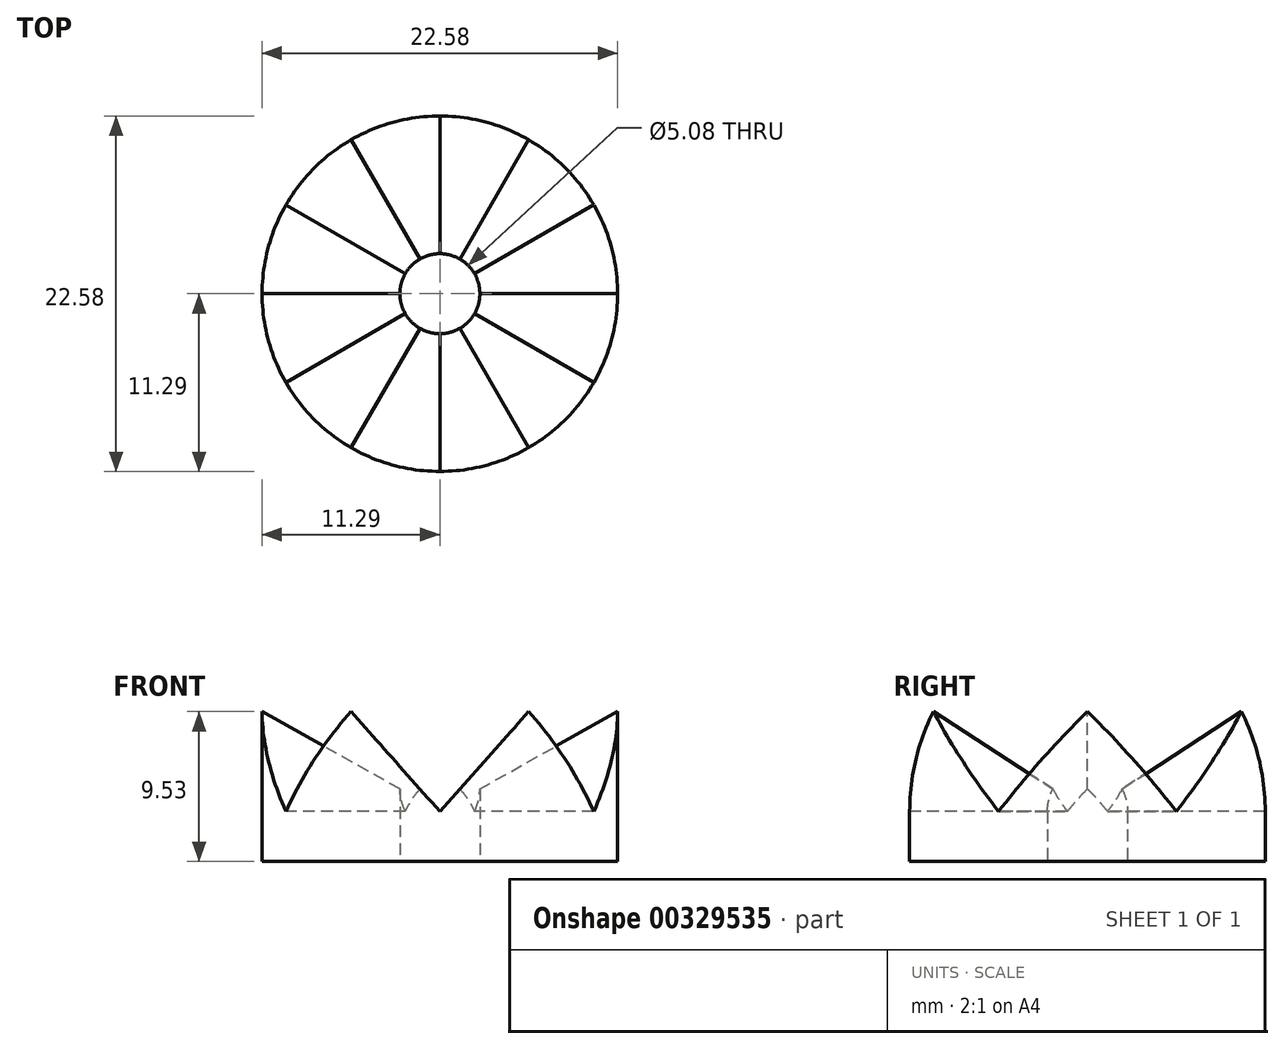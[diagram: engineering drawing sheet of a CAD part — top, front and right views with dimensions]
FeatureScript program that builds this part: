
annotation { "Feature Type Name" : "Feature", "Feature Type Description" : "" }
export const myFeature = defineFeature(function(context is Context, id is Id, definition is map)
    precondition{}
    {
        {
            var Q0;
            Q0=qCreatedBy(makeId("Top.planeOp"),FACE);
            var sketch = newSketch(context, id + "F0", { "sketchPlane" : qUnion([Q0])});
            skCircle(sketch, "E0.cCircle", {"center": v(0, 0) * mm, "radius": 11.3 * mm, "construction": true});
            skLineSegment(sketch, "E0.0", {"start": v(11.3, 0) * mm, "end": v(5.65, -9.78) * mm});
            skLineSegment(sketch, "E0.1", {"start": v(5.65, -9.78) * mm, "end": v(-5.65, -9.78) * mm});
            skLineSegment(sketch, "E0.2", {"start": v(-5.65, -9.78) * mm, "end": v(-11.3, 0) * mm});
            skLineSegment(sketch, "E0.3", {"start": v(-11.3, 0) * mm, "end": v(-5.65, 9.78) * mm});
            skLineSegment(sketch, "E0.4", {"start": v(-5.65, 9.78) * mm, "end": v(5.65, 9.78) * mm});
            skLineSegment(sketch, "E0.5", {"start": v(5.65, 9.78) * mm, "end": v(11.3, 0) * mm});
            skLineSegment(sketch, "E1", {"start": v(-5.65, -9.78) * mm, "end": v(5.65, 9.78) * mm});
            skLineSegment(sketch, "E2", {"start": v(11.3, 0) * mm, "end": v(-11.3, 0) * mm});
            skLineSegment(sketch, "E3", {"start": v(5.65, -9.78) * mm, "end": v(-5.65, 9.78) * mm});
            skCircle(sketch, "E4", {"center": v(0, 0) * mm, "radius": 11.3 * mm});
            skSolve(sketch);
        }
        {
            var Q0;
            {var subQ0=sQuery(id+"F0.wireOp",EDGE,"E0.3");Q0=makeQuery(id+"F0.imprint","IMPRINT",FACE,{"disambiguationData":[TD([[makeQuery(id+"F0.imprint","IMPRINT",EDGE,{"derivedFrom":subQ0}),-1.0]])]});}
            var Q1;
            {var subQ0=sQuery(id+"F0.wireOp",EDGE,"E0.2");Q1=makeQuery(id+"F0.imprint","IMPRINT",FACE,{"disambiguationData":[TD([[makeQuery(id+"F0.imprint","IMPRINT",EDGE,{"derivedFrom":subQ0}),-1.0]])]});}
            var Q2;
            {var subQ0=sQuery(id+"F0.wireOp",EDGE,"E0.1");Q2=makeQuery(id+"F0.imprint","IMPRINT",FACE,{"disambiguationData":[TD([[makeQuery(id+"F0.imprint","IMPRINT",EDGE,{"derivedFrom":subQ0}),-1.0]])]});}
            var Q3;
            {var subQ0=sQuery(id+"F0.wireOp",EDGE,"E0.5");Q3=makeQuery(id+"F0.imprint","IMPRINT",FACE,{"disambiguationData":[TD([[makeQuery(id+"F0.imprint","IMPRINT",EDGE,{"derivedFrom":subQ0}),-1.0]])]});}
            var Q4;
            {var subQ0=sQuery(id+"F0.wireOp",EDGE,"E0.0");Q4=makeQuery(id+"F0.imprint","IMPRINT",FACE,{"disambiguationData":[TD([[makeQuery(id+"F0.imprint","IMPRINT",EDGE,{"derivedFrom":subQ0}),-1.0]])]});}
            var Q5;
            {var subQ0=sQuery(id+"F0.wireOp",EDGE,"E0.4");Q5=makeQuery(id+"F0.imprint","IMPRINT",FACE,{"disambiguationData":[TD([[makeQuery(id+"F0.imprint","IMPRINT",EDGE,{"derivedFrom":subQ0}),-1.0]])]});}
            extrude(context, id + "F1", {"entities" : qUnion([Q0, Q1, Q2, Q3, Q4, Q5]), "depth" : 6.35 * mm, "hasSecondDirection" : true, "secondDirectionOppositeDirection" : true, "secondDirectionDepth" : 3.17 * mm});
        }
        {
            var Q0;
            Q0=makeQuery(id+"F1.opExtrude","SWEPT_FACE",FACE,{"disambiguationData":[OSD([sQuery(id+"F0.wireOp",EDGE,"E0.1")])]});
            var sketch = newSketch(context, id + "F2", { "sketchPlane" : qUnion([Q0])});
            skLineSegment(sketch, "E5", {"start": v(0, 6.35) * mm, "end": v(0, 0) * mm});
            skLineSegment(sketch, "E6", {"start": v(0, 0) * mm, "end": v(5.65, 6.35) * mm});
            skLineSegment(sketch, "E7", {"start": v(5.65, 6.35) * mm, "end": v(0, 0) * mm});
            skLineSegment(sketch, "E8", {"start": v(-5.65, 6.35) * mm, "end": v(0, 0) * mm});
            skSolve(sketch);
        }
        {
            var Q0;
            {var subQ0=sQuery(id+"F2.wireOp",EDGE,"E5");Q0=makeQuery(id+"F2.imprint","IMPRINT",FACE,{"disambiguationData":[TD([[makeQuery(id+"F2.imprint","IMPRINT",EDGE,{"derivedFrom":subQ0}),1.0]])]});}
            var Q1;
            {var subQ0=sQuery(id+"F2.wireOp",EDGE,"E5");Q1=makeQuery(id+"F2.imprint","IMPRINT",FACE,{"disambiguationData":[TD([[makeQuery(id+"F2.imprint","IMPRINT",EDGE,{"derivedFrom":subQ0}),-1.0]])]});}
            extrude(context, id + "F3", {"entities" : qUnion([Q0, Q1]), "operationType" : NewBodyOperationType.REMOVE, "endBound" : BoundingType.THROUGH_ALL, "oppositeDirection" : true, "depth" : 25.4 * mm, "hasSecondDirection" : true, "secondDirectionBound" : SecondDirectionBoundingType.THROUGH_ALL, "secondDirectionOppositeDirection" : false, "secondDirectionDepth" : 25.4 * mm});
        }
        {
            var Q0;
            Q0=makeQuery(id+"F1.opExtrude","SWEPT_FACE",FACE,{"disambiguationData":[OSD([sQuery(id+"F0.wireOp",EDGE,"E0.2")])]});
            var sketch = newSketch(context, id + "F4", { "sketchPlane" : qUnion([Q0])});
            skLineSegment(sketch, "E9", {"start": v(0, 6.35) * mm, "end": v(0, 0) * mm});
            skLineSegment(sketch, "E10", {"start": v(0, 0) * mm, "end": v(5.65, 6.35) * mm});
            skLineSegment(sketch, "E11", {"start": v(5.65, 6.35) * mm, "end": v(-5.65, 6.35) * mm});
            skLineSegment(sketch, "E12", {"start": v(-5.65, 6.35) * mm, "end": v(0, 0) * mm});
            skSolve(sketch);
        }
        {
            var Q0;
            Q0=qSketchRegion(id+"F4",true);
            extrude(context, id + "F5", {"entities" : qUnion([Q0]), "operationType" : NewBodyOperationType.REMOVE, "endBound" : BoundingType.THROUGH_ALL, "oppositeDirection" : true, "depth" : 25.4 * mm, "hasSecondDirection" : true, "secondDirectionBound" : SecondDirectionBoundingType.THROUGH_ALL, "secondDirectionOppositeDirection" : false, "secondDirectionDepth" : 25.4 * mm});
        }
        {
            var Q0;
            Q0=makeQuery(id+"F1.opExtrude","SWEPT_FACE",FACE,{"disambiguationData":[OSD([sQuery(id+"F0.wireOp",EDGE,"E0.3")])]});
            var sketch = newSketch(context, id + "F6", { "sketchPlane" : qUnion([Q0])});
            skLineSegment(sketch, "E13", {"start": v(0, 6.35) * mm, "end": v(0, 0) * mm});
            skPoint(sketch, "E13.endSnap0", {"position": v(0, 6.35) * mm});
            skLineSegment(sketch, "E14", {"start": v(0, 0) * mm, "end": v(5.65, 6.35) * mm});
            skLineSegment(sketch, "E15", {"start": v(5.65, 6.35) * mm, "end": v(0, 0) * mm});
            skLineSegment(sketch, "E16", {"start": v(-5.65, 6.35) * mm, "end": v(0, 0) * mm});
            skSolve(sketch);
        }
        {
            var Q0;
            {var subQ0=sQuery(id+"F6.wireOp",EDGE,"E13");Q0=makeQuery(id+"F6.imprint","IMPRINT",FACE,{"disambiguationData":[TD([[makeQuery(id+"F6.imprint","IMPRINT",EDGE,{"derivedFrom":subQ0}),1.0]])]});}
            var Q1;
            {var subQ0=sQuery(id+"F6.wireOp",EDGE,"E13");Q1=makeQuery(id+"F6.imprint","IMPRINT",FACE,{"disambiguationData":[TD([[makeQuery(id+"F6.imprint","IMPRINT",EDGE,{"derivedFrom":subQ0}),-1.0]])]});}
            extrude(context, id + "F7", {"entities" : qUnion([Q0, Q1]), "operationType" : NewBodyOperationType.REMOVE, "endBound" : BoundingType.THROUGH_ALL, "oppositeDirection" : true, "depth" : 25.4 * mm, "hasSecondDirection" : true, "secondDirectionBound" : SecondDirectionBoundingType.THROUGH_ALL, "secondDirectionOppositeDirection" : false, "secondDirectionDepth" : 25.4 * mm});
        }
        {
            var Q0;
            {var subQ0=sQuery(id+"F0.wireOp",EDGE,"E0.3");Q0=makeQuery(id+"F0.imprint","IMPRINT",FACE,{"disambiguationData":[TD([[makeQuery(id+"F0.imprint","IMPRINT",EDGE,{"derivedFrom":subQ0}),1.0]])]});}
            var Q1;
            {var subQ0=sQuery(id+"F0.wireOp",EDGE,"E0.4");Q1=makeQuery(id+"F0.imprint","IMPRINT",FACE,{"disambiguationData":[TD([[makeQuery(id+"F0.imprint","IMPRINT",EDGE,{"derivedFrom":subQ0}),1.0]])]});}
            var Q2;
            {var subQ0=sQuery(id+"F0.wireOp",EDGE,"E0.1");Q2=makeQuery(id+"F0.imprint","IMPRINT",FACE,{"disambiguationData":[TD([[makeQuery(id+"F0.imprint","IMPRINT",EDGE,{"derivedFrom":subQ0}),1.0]])]});}
            var Q3;
            {var subQ0=sQuery(id+"F0.wireOp",EDGE,"E0.2");Q3=makeQuery(id+"F0.imprint","IMPRINT",FACE,{"disambiguationData":[TD([[makeQuery(id+"F0.imprint","IMPRINT",EDGE,{"derivedFrom":subQ0}),1.0]])]});}
            var Q4;
            {var subQ0=sQuery(id+"F0.wireOp",EDGE,"E0.0");Q4=makeQuery(id+"F0.imprint","IMPRINT",FACE,{"disambiguationData":[TD([[makeQuery(id+"F0.imprint","IMPRINT",EDGE,{"derivedFrom":subQ0}),1.0]])]});}
            var Q5;
            {var subQ0=sQuery(id+"F0.wireOp",EDGE,"E0.5");Q5=makeQuery(id+"F0.imprint","IMPRINT",FACE,{"disambiguationData":[TD([[makeQuery(id+"F0.imprint","IMPRINT",EDGE,{"derivedFrom":subQ0}),1.0]])]});}
            extrude(context, id + "F8", {"entities" : qUnion([Q0, Q1, Q2, Q3, Q4, Q5]), "operationType" : NewBodyOperationType.ADD, "depth" : 6.35 * mm, "hasSecondDirection" : true, "secondDirectionOppositeDirection" : true, "secondDirectionDepth" : 3.17 * mm});
        }
        {
            var Q0;
            Q0=makeQuery(id+"F8.opExtrude","SWEPT_FACE",FACE,{"disambiguationData":[OSD([sQuery(id+"F0.wireOp",EDGE,"E0.3")])]});
            extrude(context, id + "F9", {"entities" : qUnion([Q0]), "operationType" : NewBodyOperationType.REMOVE, "oppositeDirection" : true, "depth" : 25.4 * mm});
        }
        {
            var Q0;
            Q0=makeQuery(id+"F8.opExtrude","SWEPT_FACE",FACE,{"disambiguationData":[OSD([sQuery(id+"F0.wireOp",EDGE,"E0.4")])]});
            extrude(context, id + "F10", {"entities" : qUnion([Q0]), "operationType" : NewBodyOperationType.REMOVE, "oppositeDirection" : true, "depth" : 25.4 * mm});
        }
        {
            var Q0;
            Q0=makeQuery(id+"F8.opExtrude","SWEPT_FACE",FACE,{"disambiguationData":[OSD([sQuery(id+"F0.wireOp",EDGE,"E0.5")])]});
            extrude(context, id + "F11", {"entities" : qUnion([Q0]), "operationType" : NewBodyOperationType.REMOVE, "oppositeDirection" : true, "depth" : 25.4 * mm});
        }
        {
            var Q0;
            Q0=makeQuery(id+"F8.opExtrude","SWEPT_FACE",FACE,{"disambiguationData":[OSD([sQuery(id+"F0.wireOp",EDGE,"E0.2")])]});
            extrude(context, id + "F12", {"entities" : qUnion([Q0]), "operationType" : NewBodyOperationType.REMOVE, "oppositeDirection" : true, "depth" : 25.4 * mm});
        }
        {
            var Q0;
            Q0=makeQuery(id+"F8.opExtrude","SWEPT_FACE",FACE,{"disambiguationData":[OSD([sQuery(id+"F0.wireOp",EDGE,"E0.1")])]});
            extrude(context, id + "F13", {"entities" : qUnion([Q0]), "operationType" : NewBodyOperationType.REMOVE, "oppositeDirection" : true, "depth" : 25.4 * mm});
        }
        {
            var Q0;
            Q0=makeQuery(id+"F8.opExtrude","SWEPT_FACE",FACE,{"disambiguationData":[OSD([sQuery(id+"F0.wireOp",EDGE,"E0.0")])]});
            extrude(context, id + "F14", {"entities" : qUnion([Q0]), "operationType" : NewBodyOperationType.REMOVE, "oppositeDirection" : true, "depth" : 25.4 * mm});
        }
        {
            var Q0;
            {var subQ0=sQuery(id+"F0.wireOp",EDGE,"E4");var subQ1=sQuery(id+"F0.wireOp",EDGE,"E0.5");var subQ2=sQuery(id+"F0.wireOp",EDGE,"E0.4");var subQ3=sQuery(id+"F0.wireOp",EDGE,"E0.3");var subQ4=sQuery(id+"F0.wireOp",EDGE,"E0.2");var subQ5=sQuery(id+"F0.wireOp",EDGE,"E0.1");var subQ6=sQuery(id+"F0.wireOp",EDGE,"E0.0");Q0=makeQuery(id+"F8.boolean.opBoolean","MERGE",FACE,{"derivedFrom":[makeQuery(id+"F1.opExtrude","CAP_FACE",FACE,{"disambiguationData":[OSD([subQ6,subQ5,subQ4,subQ3,subQ2,subQ1])],"isStart":true}),makeQuery(id+"F8.opExtrude","CAP_FACE",FACE,{"disambiguationData":[OSD([subQ6,subQ0])],"isStart":true}),makeQuery(id+"F8.opExtrude","CAP_FACE",FACE,{"disambiguationData":[OSD([subQ5,subQ0])],"isStart":true}),makeQuery(id+"F8.opExtrude","CAP_FACE",FACE,{"disambiguationData":[OSD([subQ4,subQ0])],"isStart":true}),makeQuery(id+"F8.opExtrude","CAP_FACE",FACE,{"disambiguationData":[OSD([subQ3,subQ0])],"isStart":true}),makeQuery(id+"F8.opExtrude","CAP_FACE",FACE,{"disambiguationData":[OSD([subQ2,subQ0])],"isStart":true}),makeQuery(id+"F8.opExtrude","CAP_FACE",FACE,{"disambiguationData":[OSD([subQ1,subQ0])],"isStart":true})]});}
            var sketch = newSketch(context, id + "F15", { "sketchPlane" : qUnion([Q0])});
            skCircle(sketch, "E17", {"center": v(0, 0) * mm, "radius": 2.54 * mm});
            skSolve(sketch);
        }
        {
            var Q0;
            Q0 = qSketchRegion(id + "F15", true);
            extrude(context, id + "F16", {"entities" : qUnion([Q0]), "operationType" : NewBodyOperationType.REMOVE, "endBound" : BoundingType.THROUGH_ALL, "oppositeDirection" : true, "depth" : 25.4 * mm});
        }
    });
